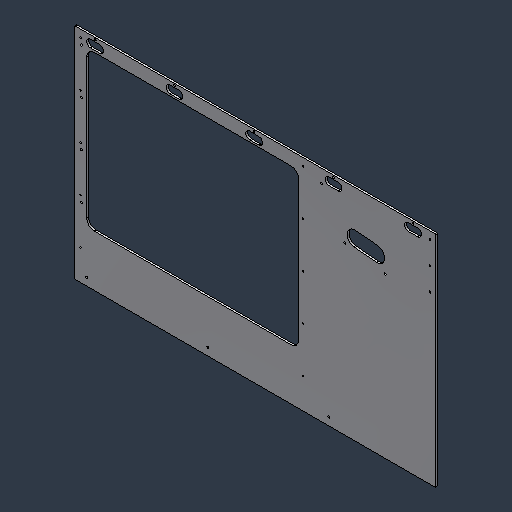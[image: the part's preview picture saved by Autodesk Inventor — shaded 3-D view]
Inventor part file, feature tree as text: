
AUTODESK INVENTOR PART (.ipt)
format: ipt  version: 2024.3 (Build 283343000, 343)  size: 141,312 bytes
history: native  units: mm (DEFAULTED — no unit token found)
features: fillet x1
ambient origin geometry x8: Origin, YZ Plane, XZ Plane, XY Plane, X Axis, Y Axis, Z Axis, Center Point
bodies: Solid1 (feature_tree)
feature tree (1):
  fillet  "Fillet2"  [1 undecoded]
note: 1 required parameter value undecoded (feature->parameter linkage not recoverable at this tier; creation-order binding heuristic only, values carry confidence <= 0.55)
